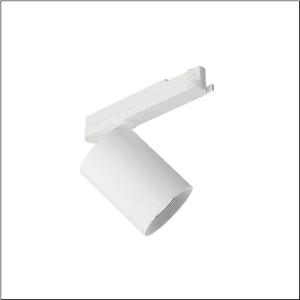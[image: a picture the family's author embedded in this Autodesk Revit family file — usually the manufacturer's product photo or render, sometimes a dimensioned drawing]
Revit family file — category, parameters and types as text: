
# Revit family: spot_11_51sd14mbb5a
name_source: partatom
category: Lighting Fixtures
units: mm (PartAtom-declared; Revit-internal decimal feet)

## family parameters
Cut with Voids When Loaded = No
Host = Face
Light Source = No
Part Type = Normal
Room Calculation Point = No
Round Connector Dimension = Use Diameter
Shared = No

## types (1)
- --- (1 x LED, 7340 lm, 50.2 W, 3000K)
    Apparent Load = 50 VA
    CIE Flux Codes = 95 98 100 100 100
    Color Rendering = 90
    Color Temperature = 3000K
    Default Elevation = 1800 mm
    Description = Spot 11, directional spotlight, light control with lens, of PMMA, LED rated luminous flux: 5.630lm, light colour: 930, control gear: ECG Multilumen, with 3-phase adapter, mains connection: 220..240V, AC, 50/60Hz, of aluminium, traffic white (RAL 9016), length: 213mm, diameter: 105mm, protection rating (complete): IP20, insulation class (complete): insulation class I (protective earthing), certification: CE, impact resistance: IK02, permissible ambient temperature for indoor applications: -20..+40°C, packaging unit: 1 piece
    Height = 175 mm
    Lamp = 1 x LED
    Lamp Light Flux = 7340 lm
    Lamp Power = 50.2 W
    Lamp count = 1
    Length = 105 mm
    Luminous efficacy = 146 lm/W
    Manufacturer = Siteco
    ModVariant = No
    Model = 51SD14MBB5A
    Mounting Place = Ceiling
    Mounting Type = Pendant
    Number of Poles = 1
    OnlyDefault = Yes
    Power Factor = 1
    Product Name = Spot 11
    Product group = directional spotlight
    ProductGroupID = 905
    Protection Class = Protection class I
    Protection Degree = IP 20
    RLX_Detail_Level = 1
    RLX_Emergency_Light_Flux = 0 lm
    RLX_Emergency_Type = 0
    RLX_Emergency_Type_DB = No
    RlxData = <blob elided: 17689 chars, md5=3da4d45c>
    Socket = socket
    Standby Power = 0 W
    System Light Flux = 7340 lm
    System Power = 50 W
    Type Comments = factory setting: luminous flux: 100 % | (ON | ON | ON | ON) | 1050 mA
    Type Image = l_1006697.jpg
    URL = http://relux.com
    VarID = @adj_097639
    Voltage = 0 V
    Weight = 0.00 kg
    Width = 0 mm  [stored 0 ft]

note: [stored X ft] marks values corroborated as IEEE doubles in the binary element streams (Revit-internal decimal feet)

## geometry (parser evidence)
native form markers: Blend x4, Sweep x10
no freeform markers — native parametric forms only
